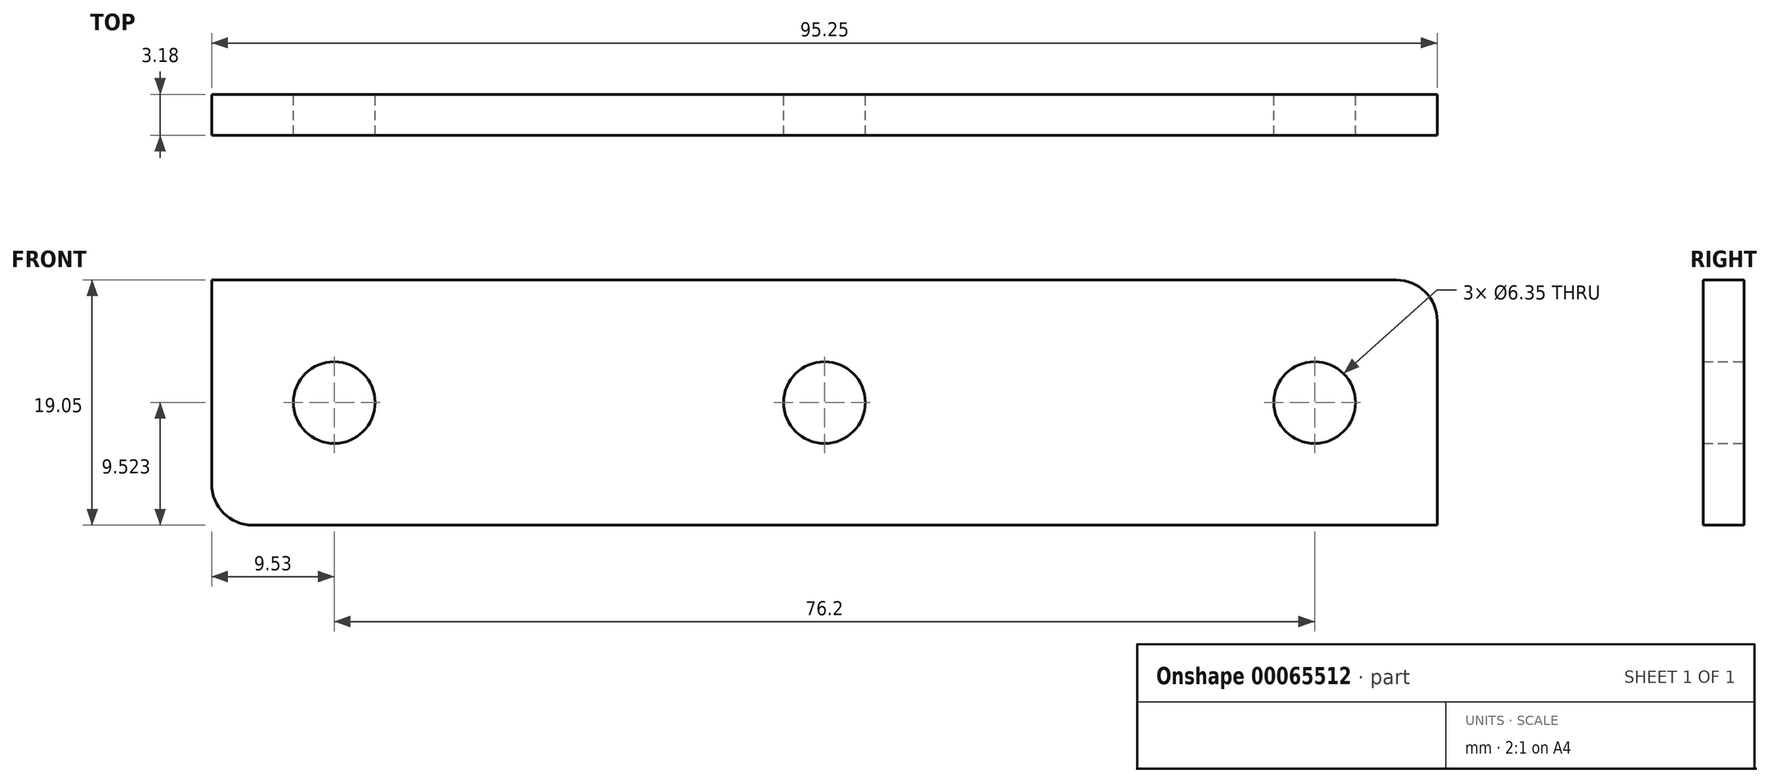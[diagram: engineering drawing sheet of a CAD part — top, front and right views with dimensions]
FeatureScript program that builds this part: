
annotation { "Feature Type Name" : "Feature", "Feature Type Description" : "" }
export const myFeature = defineFeature(function(context is Context, id is Id, definition is map)
    precondition{}
    {
        {
            var Q0;
            Q0=qCreatedBy(makeId("Front.planeOp"),FACE);
            var sketch = newSketch(context, id + "F0", { "sketchPlane" : qUnion([Q0])});
            skLineSegment(sketch, "E0.bottom", {"start": v(31.55, -3.5) * mm, "end": v(126.8, -3.5) * mm});
            skLineSegment(sketch, "E0.top", {"start": v(31.55, -22.55) * mm, "end": v(126.8, -22.55) * mm});
            skLineSegment(sketch, "E0.left", {"start": v(31.55, -3.5) * mm, "end": v(31.55, -22.55) * mm});
            skLineSegment(sketch, "E0.right", {"start": v(126.8, -3.5) * mm, "end": v(126.8, -22.55) * mm});
            skLineSegment(sketch, "E1.bottom", {"start": v(31.55, -3.5) * mm, "end": v(41.08, -3.5) * mm});
            skLineSegment(sketch, "E1.top", {"start": v(31.55, -13.03) * mm, "end": v(41.08, -13.03) * mm});
            skLineSegment(sketch, "E1.left", {"start": v(31.55, -3.5) * mm, "end": v(31.55, -13.03) * mm});
            skLineSegment(sketch, "E1.right", {"start": v(41.08, -3.5) * mm, "end": v(41.08, -13.03) * mm});
            skLineSegment(sketch, "E2.bottom", {"start": v(126.8, -22.55) * mm, "end": v(117.28, -22.55) * mm});
            skLineSegment(sketch, "E2.top", {"start": v(126.8, -13.03) * mm, "end": v(117.28, -13.03) * mm});
            skLineSegment(sketch, "E2.left", {"start": v(126.8, -22.55) * mm, "end": v(126.8, -13.03) * mm});
            skLineSegment(sketch, "E2.right", {"start": v(117.28, -22.55) * mm, "end": v(117.28, -13.03) * mm});
            skCircle(sketch, "E3", {"center": v(41.08, -13.03) * mm, "radius": 3.18 * mm});
            skCircle(sketch, "E4", {"center": v(117.28, -13.03) * mm, "radius": 3.18 * mm});
            skLineSegment(sketch, "E5", {"start": v(79.18, -3.5) * mm, "end": v(79.18, -22.55) * mm});
            skCircle(sketch, "E6", {"center": v(79.18, -13.03) * mm, "radius": 3.18 * mm});
            skSolve(sketch);
        }
        {
            var Q0;
            Q0 = qSketchRegion(id + "F0", true);
            extrude(context, id + "F1", {"entities" : qUnion([Q0]), "depth" : 3.17 * mm});
        }
        {
            var Q0;
            Q0=makeQuery(id+"F1.opExtrude","SWEPT_EDGE",EDGE,{"disambiguationData":[OSD([sQuery(id+"F0.wireOp",EDGE,"E1.bottom"),sQuery(id+"F0.wireOp",EDGE,"E1.left")])]});
            var Q1;
            Q1=makeQuery(id+"F1.opExtrude","SWEPT_EDGE",EDGE,{"disambiguationData":[OSD([sQuery(id+"F0.wireOp",EDGE,"E0.top"),sQuery(id+"F0.wireOp",EDGE,"E0.left")])]});
            var Q2;
            Q2=makeQuery(id+"F1.opExtrude","SWEPT_EDGE",EDGE,{"disambiguationData":[OSD([sQuery(id+"F0.wireOp",EDGE,"E0.bottom"),sQuery(id+"F0.wireOp",EDGE,"E0.right")])]});
            var Q3;
            Q3=makeQuery(id+"F1.opExtrude","SWEPT_EDGE",EDGE,{"disambiguationData":[OSD([sQuery(id+"F0.wireOp",EDGE,"E2.bottom"),sQuery(id+"F0.wireOp",EDGE,"E2.left")])]});
            fillet(context, id + "F2", {"entities" : qUnion([Q0, Q1, Q2, Q3]), "radius" : 3.17 * mm, "tangentPropagation" : true, "allowEdgeOverflow" : false});
        }
    });
